# Revit family: Steni - Panel - Nature Type C Tumbled
name_source: partatom
category: Generic Models
revit_build: Autodesk Revit MEP 2012 (Build: 20110309_2315(x64)
units: mm (PartAtom-declared; Revit-internal decimal feet)

## types (1)
- Steni - Panel - Nature Type C Tumbled
    Allowable Variation = ± 2 mm
    BIMobject Category = Cladding
    BIMobject QR code url = http://steni.bimobject.com
    Bending Stiffness = Nm²/m
    Density = Apprx. 2000 Kg/m³
    Design country = Norway
    Diagonal Deviation = 3 mm
    Drilling Distance Tolerance = ± 5 mm
    Edge Straightness Full Size = 1 mm
    Edition number = 1
    Elasticity Module = 5000 MPa
    Flexural Strength = 40 MPa
    Hardness Of Aggregate = SEE SPEC.
    Heat Conductivity = 0.55 W/m°C
    Heat Resistance = 0.0074 m²°C/W
    Humidity Altered Dimension = 5.2 X 106 m/m x%RF
    IFC Classification = Covering
    Impact Strength = 20 KJ / m 2
    Impermeability = 100%
    Installation instructions = http://steni.com
    Manufacturer = Steni
    Manufacturer URL = www.steni.com
    Manufacturer country = Norway
    Model = Steni - Panel - Nature Type C Tumbled
    Name of the object = Steni - Panel - Nature Type C Tumbled
    No Damage = 300 CYCLE
    NominalHeight = 1195
    NominalWidth = 3500
    Penetration Of Water Vapour = 3,3 X 10-12 Kg/m²sPa
    Product SKU = sc123
    Product data url = http://steni.com
    Product family = Steni Nature
    Product group = FS 100
    Riverse Side = PLANE
    Rupture Factor Per M = 288 Nm/m
    Size Of Aggregate Particle = 6-12mm
    Standard Length = 3500 mm  [stored 11.4829 ft]
    Standard Width = 1195 mm  [stored 3.9206 ft]
    Technical description = http://steni.com
    Temperature Expansion (-20° +65°) = 0.026 mm/m°C
    Tensile Strength = 15 N/mm²
    Thickness 2 = Apprx. 14 ,mm
    Type Of Aggregate = SEE SPEC.
    UNSPC Category = Siding and exterior wall materials
    UNSPC code = 301518
    URL = http://steni.bimobject.com
    Uniclass 1.4 Code = L381
    Uniclass 1.4 Description = Facades and roofs
    Water Absorbtion After 24 Hrs = 0.5%
    Water Absorbtion After 28 days = <1.5 %
    Weight Net (kg) = Apprx. 25 Kg/m²

note: [stored X ft] marks values corroborated as IEEE doubles in the binary element streams (Revit-internal decimal feet)

## geometry (parser evidence)
native form markers: Sweep x1
no freeform markers — native parametric forms only
